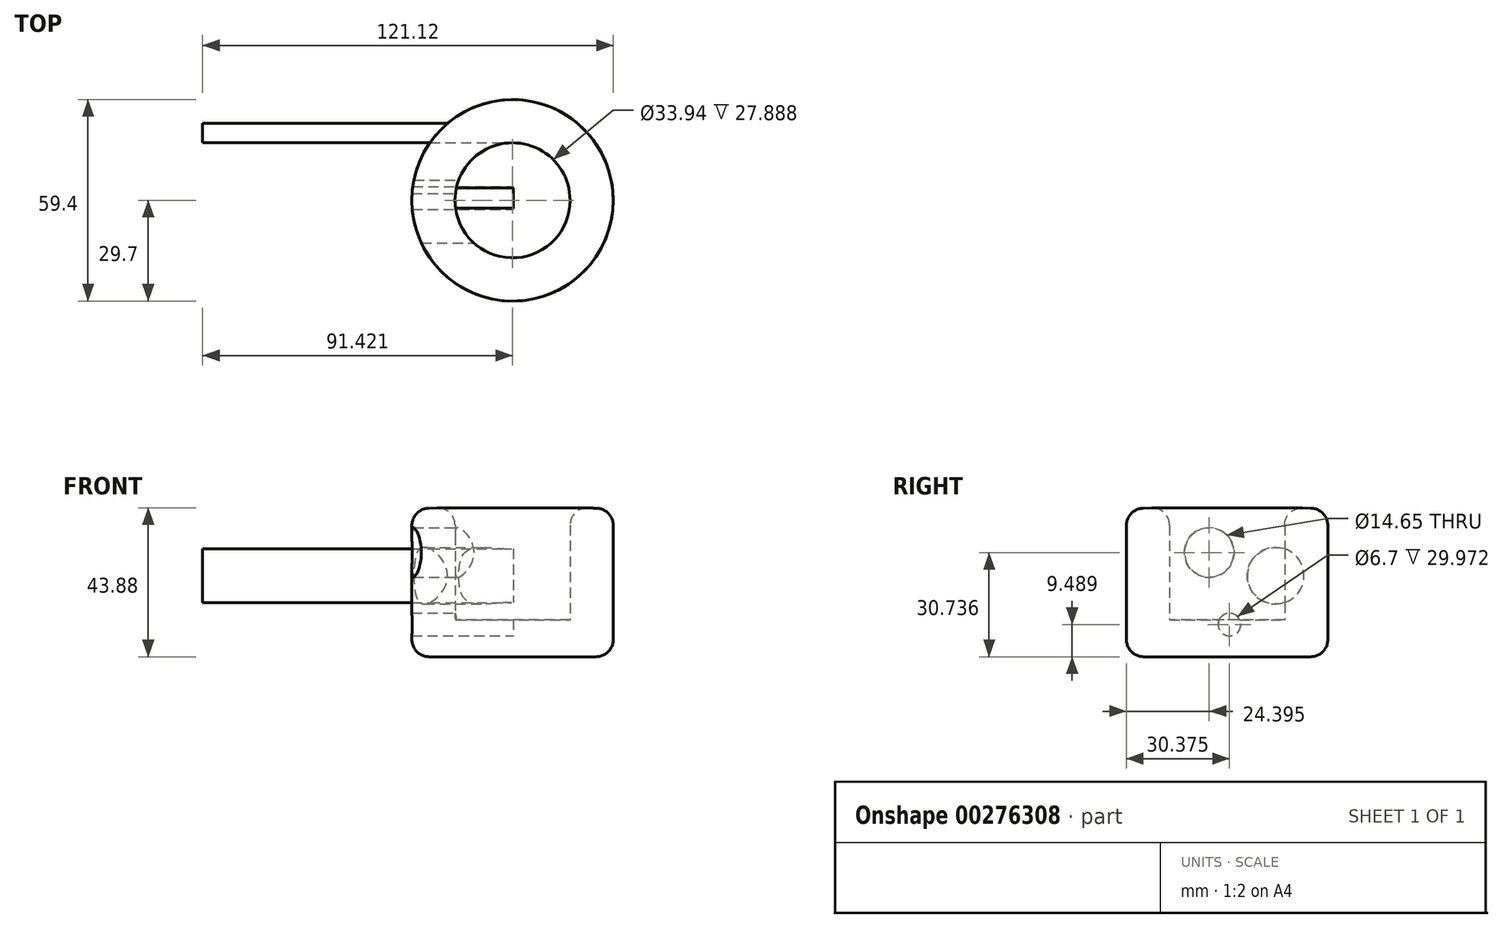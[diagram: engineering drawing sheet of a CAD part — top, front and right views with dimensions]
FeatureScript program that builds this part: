
annotation { "Feature Type Name" : "Feature", "Feature Type Description" : "" }
export const myFeature = defineFeature(function(context is Context, id is Id, definition is map)
    precondition{}
    {
        {
            var Q0;
            Q0=qCreatedBy(makeId("Front.planeOp"),FACE);
            var sketch = newSketch(context, id + "F0", { "sketchPlane" : qUnion([Q0])});
            skLineSegment(sketch, "E0", {"start": v(0, 43.64) * mm, "end": v(0, 0) * mm});
            skLineSegment(sketch, "E1", {"start": v(0, 0) * mm, "end": v(29.7, 0) * mm});
            skLineSegment(sketch, "E2", {"start": v(29.7, 0) * mm, "end": v(29.7, 10.91) * mm});
            skLineSegment(sketch, "E3", {"start": v(29.7, 10.91) * mm, "end": v(12.73, 10.91) * mm});
            skLineSegment(sketch, "E4", {"start": v(12.73, 10.91) * mm, "end": v(12.73, 44.05) * mm});
            skLineSegment(sketch, "E5", {"start": v(12.93, 44.05) * mm, "end": v(0, 43.64) * mm});
            skSolve(sketch);
        }
        {
            var Q0;
            {var subQ1=sQuery(id+"F0.wireOp",EDGE,"E0");Q0=makeQuery(id+"F0.imprint","IMPRINT",FACE,{"disambiguationData":[TD([[makeQuery(id+"F0.imprint","IMPRINT",EDGE,{"derivedFrom":subQ1}),1.0]])]});}
            var Q1;
            Q1=sQuery(id+"F0.wireOp",EDGE,"E2");
            revolve(context, id + "F1", {"entities" : qUnion([Q0]), "axis" : qUnion([Q1]), "revolveType" : RevolveType.FULL});
        }
        {
            var Q0;
            Q0=makeQuery(id+"F1.opRevolve","SWEPT_EDGE",EDGE,{"disambiguationData":[OSD([sQuery(id+"F0.wireOp",EDGE,"E0"),sQuery(id+"F0.wireOp",EDGE,"E5")])]});
            var Q1;
            Q1=makeQuery(id+"F1.opRevolve","SWEPT_EDGE",EDGE,{"disambiguationData":[OSD([sQuery(id+"F0.wireOp",EDGE,"E4"),sQuery(id+"F0.wireOp",EDGE,"E5")])]});
            var Q2;
            Q2=makeQuery(id+"F1.opRevolve","SWEPT_EDGE",EDGE,{"disambiguationData":[OSD([sQuery(id+"F0.wireOp",EDGE,"E0"),sQuery(id+"F0.wireOp",EDGE,"E1")])]});
            var Q3;
            Q3=makeQuery(id+"F1.opRevolve","SWEPT_FACE",FACE,{"disambiguationData":[OSD([sQuery(id+"F0.wireOp",EDGE,"E1")])]});
            fillet(context, id + "F2", {"entities" : qUnion([Q0, Q1, Q2, Q3]), "radius" : 5.08 * mm, "tangentPropagation" : true, "allowEdgeOverflow" : false});
        }
        {
            var Q0;
            Q0=qCreatedBy(makeId("Right.planeOp"),FACE);
            cPlane(context, id + "F3", {"entities" : qUnion([Q0]), "cplaneType" : CPlaneType.OFFSET, "offset" : 29.97 * mm, "width" : 152.4 * mm, "height" : 152.4 * mm});
        }
        {
            var Q0;
            Q0=qCreatedBy(id+"F3.planeOp",FACE);
            var sketch = newSketch(context, id + "F4", { "sketchPlane" : qUnion([Q0])});
            skCircle(sketch, "E6", {"center": v(-5.3, 30.74) * mm, "radius": 7.32 * mm});
            skCircle(sketch, "E7", {"center": v(14.29, 23.89) * mm, "radius": 8.37 * mm});
            skCircle(sketch, "E8", {"center": v(0.68, 9.49) * mm, "radius": 3.35 * mm});
            skSolve(sketch);
        }
        {
            var Q0;
            Q0=makeQuery(id+"F4.imprint","IMPRINT",FACE,{"disambiguationData":[TD([[makeQuery(id+"F4.imprint","IMPRINT",EDGE,{"derivedFrom":sQuery(id+"F4.wireOp",EDGE,"E6")}),1.0]])]});
            var Q1;
            Q1=makeQuery(id+"F4.imprint","IMPRINT",FACE,{"disambiguationData":[TD([[makeQuery(id+"F4.imprint","IMPRINT",EDGE,{"derivedFrom":sQuery(id+"F4.wireOp",EDGE,"E7")}),1.0]])]});
            var Q2;
            Q2=makeQuery(id+"F4.imprint","IMPRINT",FACE,{"disambiguationData":[TD([[makeQuery(id+"F4.imprint","IMPRINT",EDGE,{"derivedFrom":sQuery(id+"F4.wireOp",EDGE,"E8")}),1.0]])]});
            extrude(context, id + "F5", {"entities" : qUnion([Q0, Q1, Q2]), "operationType" : NewBodyOperationType.REMOVE, "oppositeDirection" : true, "depth" : 50.8 * mm});
        }
        {
            var Q0;
            Q0=makeQuery(id+"F5.boolean.opBoolean","COPY",FACE,{"derivedFrom":makeQuery(id+"F5.opExtrude","CAP_FACE",FACE,{"disambiguationData":[OSD([sQuery(id+"F4.wireOp",EDGE,"E7")])],"isStart":true})});
            extrude(context, id + "F6", {"entities" : qUnion([Q0]), "operationType" : NewBodyOperationType.ADD, "depth" : 91.7 * mm});
        }
    });
